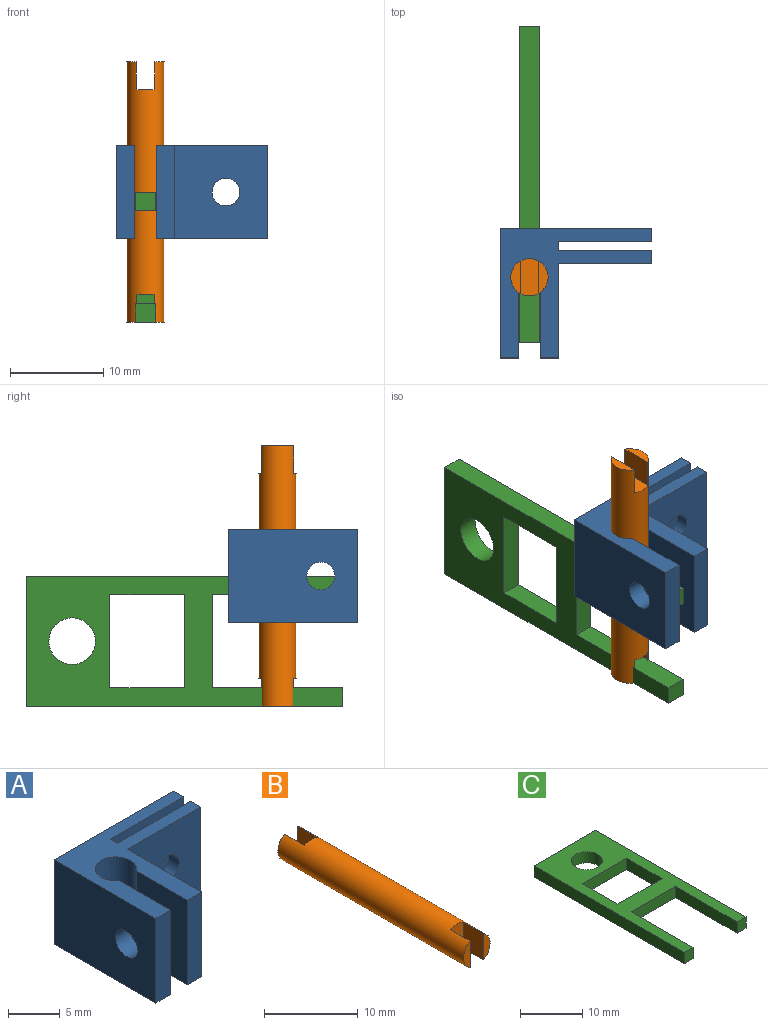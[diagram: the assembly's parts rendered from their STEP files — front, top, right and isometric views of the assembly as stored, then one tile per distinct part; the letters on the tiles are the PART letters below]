
ASSEMBLY  parts=3 mates=2
PART A: 20 faces, bbox 16.3x13.9x10 mm
  f0: plane 13.93x10mm, normal (-1,0,0), area 132.2mm2, adj f1,f13,f14,f15,f19
  f1: plane 10x2mm, normal (0,-1,0), area 20mm2, adj f0,f2,f14,f15
  f2: plane 10x7mm, normal (1,0,0), area 62.9mm2, adj f1,f3,f14,f15,f19
  f3: cylinder r=2mm len=10mm, axis (0,0,-1), area 101.2mm2, adj f2,f4,f14,f15
  f4: plane 10x7mm, normal (-1,0,0), area 62.9mm2, adj f3,f5,f14,f15,f18
  f5: plane 10x2mm, normal (0,-1,0), area 20mm2, adj f4,f6,f14,f15
  f6: plane 10.13x10mm, normal (1,0,0), area 94.2mm2, adj f5,f7,f14,f15,f18
  f7: plane 10x10mm, normal (0,-1,0), area 92.9mm2, adj f6,f8,f14,f15,f17
  f8: plane 10x1.4mm, normal (1,0,0), area 14mm2, adj f7,f9,f14,f15
  f9: plane 10x10mm, normal (0,1,0), area 92.9mm2, adj f8,f10,f14,f15,f17
  f10: plane 10x1mm, normal (1,0,0), area 10mm2, adj f9,f11,f14,f15
  f11: plane 10x10mm, normal (0,-1,0), area 92.9mm2, adj f10,f12,f14,f15,f16
  f12: plane 10x1.4mm, normal (1,0,0), area 14mm2, adj f11,f13,f14,f15
  f13: plane 16.3x10mm, normal (0,1,0), area 155.9mm2, adj f0,f12,f14,f15,f16
  f14: plane 16.3x13.93mm, normal (0,0,1), area 87.7mm2, adj f0,f1,f2,f3,f4,f5,f6,f7
  f15: plane 16.3x13.93mm, normal (0,0,-1), area 87.7mm2, adj f0,f1,f2,f3,f4,f5,f6,f7
  f16: cylinder r=1.5mm len=3mm, axis (0,1,0), area 13.2mm2, adj f11,f13
  f17: cylinder r=1.5mm len=3mm, axis (0,1,0), area 13.2mm2, adj f7,f9
  f18: cylinder r=1.5mm len=3mm, axis (-1,0,0), area 18.8mm2, adj f4,f6
  f19: cylinder r=1.5mm len=3mm, axis (-1,0,0), area 18.8mm2, adj f0,f2
PART B: 11 faces, bbox 4x28x4 mm
  f0: cylinder r=2mm len=28mm, axis (0,1,0), area 326.7mm2, adj f1,f2,f3,f4,f5,f6,f7,f8
  f1: plane 3.46x1mm, normal (0,1,0), area 2.5mm2, adj f0,f10
  f2: plane 3.46x1mm, normal (0,-1,0), area 2.5mm2, adj f0,f6
  f3: plane 3.46x1mm, normal (0,-1,0), area 2.5mm2, adj f0,f7
  f4: plane 3.46x1mm, normal (0,1,0), area 2.5mm2, adj f0,f9
  f5: plane 4x2mm, normal (0,-1,0), area 7.7mm2, adj f0,f6,f7
  f6: plane 3.46x3mm, normal (-1,0,0), area 10.4mm2, adj f0,f2,f5
  f7: plane 3.46x3mm, normal (1,0,0), area 10.4mm2, adj f0,f3,f5
  f8: plane 4x2mm, normal (0,1,0), area 7.7mm2, adj f0,f9,f10
  f9: plane 3.46x3mm, normal (1,0,0), area 10.4mm2, adj f0,f4,f8
  f10: plane 3.46x3mm, normal (-1,0,0), area 10.4mm2, adj f0,f1,f8
PART C: 15 faces, bbox 14x34x2.2 mm
  f0: plane 8x2.2mm, normal (1,0,0), area 17.6mm2, adj f1,f12,f13,f14
  f1: plane 10x2.2mm, normal (0,-1,0), area 22mm2, adj f0,f2,f13,f14
  f2: plane 8x2.2mm, normal (-1,0,0), area 17.6mm2, adj f1,f12,f13,f14
  f3: plane 14x2.2mm, normal (0,1,0), area 30.8mm2, adj f4,f11,f13,f14
  f4: plane 34x2.2mm, normal (-1,0,0), area 74.8mm2, adj f3,f5,f13,f14
  f5: plane 2.2x2mm, normal (0,-1,0), area 4.4mm2, adj f4,f6,f13,f14
  f6: plane 14x2.2mm, normal (1,0,0), area 30.8mm2, adj f5,f7,f13,f14
  f7: plane 10x2.2mm, normal (0,-1,0), area 22mm2, adj f6,f8,f13,f14
  f8: plane 14x2.2mm, normal (-1,0,0), area 30.8mm2, adj f7,f9,f13,f14
  f9: plane 2.2x2mm, normal (0,-1,0), area 4.4mm2, adj f8,f11,f13,f14
  f10: cylinder r=2.5mm len=5mm, axis (0,0,-1), area 34.6mm2, adj f13,f14
  f11: plane 34x2.2mm, normal (1,0,0), area 74.8mm2, adj f3,f9,f13,f14
  f12: plane 10x2.2mm, normal (0,1,0), area 22mm2, adj f0,f2,f13,f14
  f13: plane 34x14mm, normal (0,0,1), area 236.4mm2, adj f0,f1,f2,f3,f4,f5,f6,f7
  f14: plane 34x14mm, normal (0,0,-1), area 236.4mm2, adj f0,f1,f2,f3,f4,f5,f6,f7
PLACE A t=(-7.11,-0.24,5.07)mm
PLACE B rot(axis=(-1,0,0),90deg) t=(-10.79,0.37,-3.93)mm
PLACE C rot(axis=(0,1,0),90deg) t=(-11.89,12.83,-3.61)mm
MATE fastened C.f8 <-> B.f0  axis (0,0,1) through (-10.79,0.37,-1.93)mm
MATE fastened B.f0 <-> A.f3  axis (0,0,-1) through (-10.79,0.37,10.07)mm
